# Revit family: Mechanical_Equipment-GE-Zoneline_PTAC-AirConditioner-MakeupAir-AZ95
name_source: partatom
category: Mechanical Equipment
revit_build: Autodesk Revit 2018 (Build: 20190510_1515(x64)
units: mm (PartAtom-declared; Revit-internal decimal feet)

## family parameters
Classification = None
Cut with Voids When Loaded = No
Host = Face
OmniClass Number = 23.75.70.21.24
OmniClass Title = Air Terminal Units
Part Type = Normal
Room Calculation Point = No
Round Connector Dimension = Use Diameter
Shared = No

## types (32) — shared parameters
Apparent Load = 0 VA
Assembly Code = D3040100
Default Elevation = 4' - 0"
Description = Heat pump
Frequency = 60 Hz
Height = 1' - 4"
Housing Material = Plastic - GE - Gray
Keynote = 23 30 00
Manufacturer = GE Appliances
Number of Poles = 1
Outside Grill Material = Plastic - GE - Black
Phase = 1
Product Name = GE Zoneline® Packaged Terminal Air Conditioner (PTAC)
Product Page URL = http://products.geappliances.com
URL = https://www.geappliances.com
Version = 2018 v.1.0a
Warranty URL = https://www.geappliances.com
Width = 3' - 6"

## per-type parameters (varying)
| type | Model | Power Factor | Voltage |
| AZ65H07DAB - 208V Base Model 7k Load | AZ65H07DAB | 0.96 | 208 V |
| AZ65H07DAB - 230V Base Model 7k Load | AZ65H07DAB | 0.96 | 230 V |
| AZ65H07DAC - 208V Corrosion Prot 7k Load | AZ65H07DAC | 0.96 | 208 V |
| AZ65H07DAC - 230V Corrosion Prot 7k Load | AZ65H07DAC | 0.96 | 230 V |
| AZ65H07DAD - 208V with ICR 7k Load | AZ65H07DAD | 0.96 | 208 V |
| AZ65H07DAD - 230V with ICR 7k Load | AZ65H07DAD | 0.96 | 230 V |
| AZ65H07EAC - 265V Corrosion Prot 7k Load | AZ65H07EAC | 0.94 | 265 V |
| AZ65H07EAD - 265V with ICR 7k Load | AZ65H07EAD | 0.95 | 265 V |
| AZ65H09DAB - 208V Base Model 9k Load | AZ65H09DAB | 0.98 | 208 V |
| AZ65H09DAB - 230V Base Model 9k Load | AZ65H09DAB | 0.98 | 230 V |
| AZ65H09DAC - 208V Corrosion Prot 9k Load | AZ65H09DAC | 0.98 | 208 V |
| AZ65H09DAC - 230V Corrosion Prot 9k Load | AZ65H09DAC | 0.98 | 230 V |
| AZ65H09DAD - 208V with ICR 9k Load | AZ65H09DAD | 0.98 | 208 V |
| AZ65H09DAD - 230V with ICR 9k Load | AZ65H09DAD | 0.98 | 230 V |
| AZ65H09EAC - 265V Corrosion Prot 9k Load | AZ65H09EAC | 0.94 | 265 V |
| AZ65H09EAD - 265V with ICR 9k Load | AZ65H09EAD | 0.94 | 265 V |
| AZ65H12DAB - 208V Base Model 12k Load | AZ65H12DAB | 0.98 | 208 V |
| AZ65H12DAB - 230V Base Model 12k Load | AZ65H12DAB | 0.98 | 230 V |
| AZ65H12DAC - 208V Corrosion Prot 12k Load | AZ65H12DAC | 0.98 | 208 V |
| AZ65H12DAC - 230V Corrosion Prot 12k Load | AZ65H12DAC | 0.98 | 230 V |
| AZ65H12DAD - 208V with ICR 12k Load | AZ65H12DAD | 0.98 | 208 V |
| AZ65H12DAD - 230V with ICR 12k Load | AZ65H12DAD | 0.98 | 230 V |
| AZ65H12EAC - 265V Corrosion Prot 12k Load | AZ65H12EAC | 0.97 | 265 V |
| AZ65H12EAD - 265V with ICR 12k Load | AZ65H12EAD | 0.97 | 265 V |
| AZ65H15DAB - 208V Base Model 15k Load | AZ65H15DAB | 0.97 | 208 V |
| AZ65H15DAB - 230V Base Model 15k Load | AZ65H15DAB | 0.97 | 230 V |
| AZ65H15DAC - 208V Corrosion Prot 15k Load | AZ65H15DAC | 0.97 | 208 V |
| AZ65H15DAC - 230V Corrosion Prot 15k Load | AZ65H15DAC | 0.97 | 230 V |
| AZ65H15DAD - 208V with ICR 15k Load | AZ65H15DAD | 0.97 | 208 V |
| AZ65H15DAD - 230V with ICR 15k Load | AZ65H15DAD | 0.97 | 230 V |
| AZ65H15EAC - 265V Corrosion Prot 15k Load | AZ65H15EAC | 0.98 | 265 V |
| AZ65H15EAD - 265V with ICR 15k Load | AZ65H15EAD | 0.98 | 265 V |

## geometry (parser evidence)
native form markers: Sweep x3
no freeform markers — native parametric forms only
